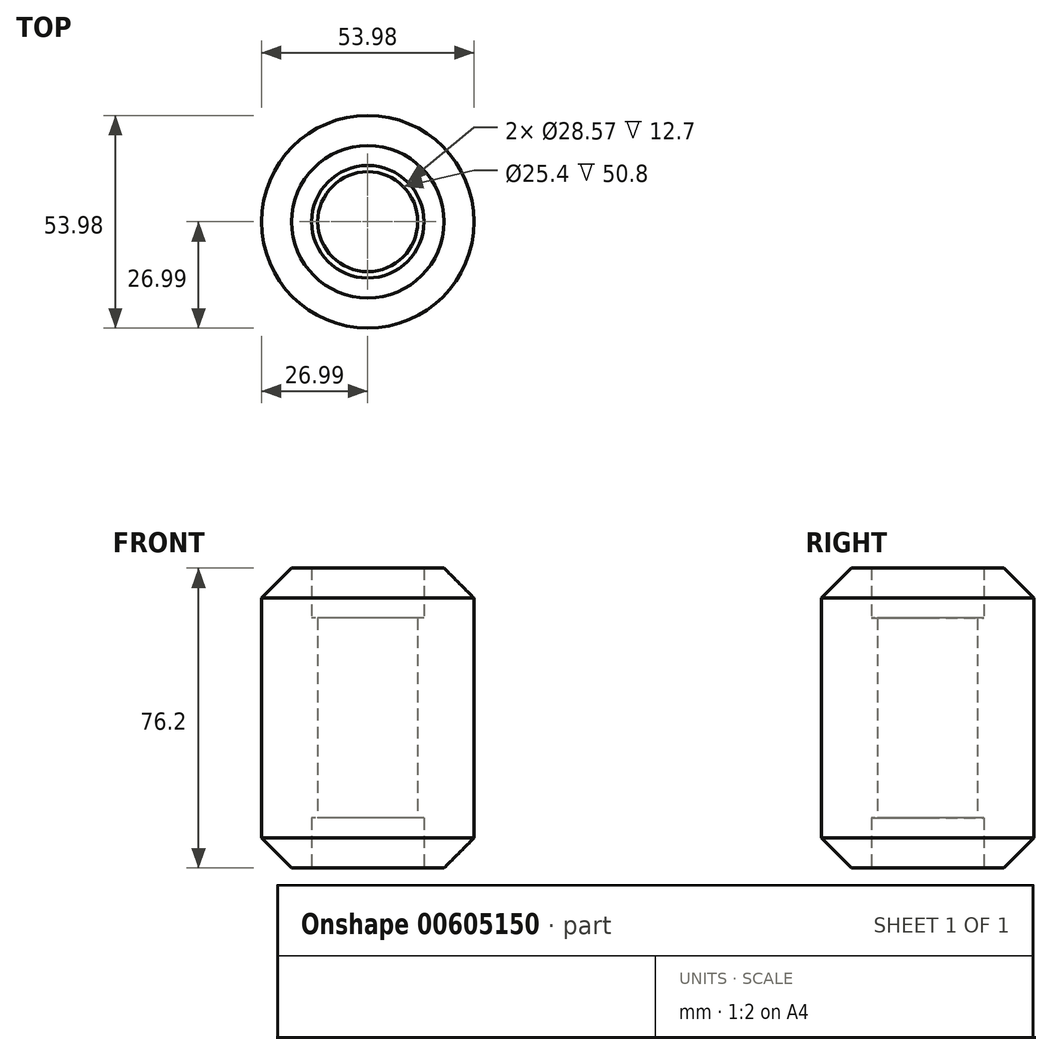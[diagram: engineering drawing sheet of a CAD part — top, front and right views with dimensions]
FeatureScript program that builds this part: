
annotation { "Feature Type Name" : "Feature", "Feature Type Description" : "" }
export const myFeature = defineFeature(function(context is Context, id is Id, definition is map)
    precondition{}
    {
        {
            var Q0;
            Q0=qCreatedBy(makeId("Top.planeOp"),FACE);
            var sketch = newSketch(context, id + "F0", { "sketchPlane" : qUnion([Q0])});
            skLineSegment(sketch, "E0", {"start": v(0, 0) * mm, "end": v(12.7, 0) * mm});
            skCircle(sketch, "E1", {"center": v(0, 0) * mm, "radius": 12.7 * mm});
            skCircle(sketch, "E2.0", {"center": v(0, 0) * mm, "radius": 14.29 * mm});
            skSolve(sketch);
        }
        {
            var Q0;
            Q0=qCreatedBy(makeId("Top.planeOp"),FACE);
            var sketch = newSketch(context, id + "F1", { "sketchPlane" : qUnion([Q0])});
            skSolve(sketch);
        }
        {
            var Q0;
            Q0=qSketchRegion(id+"F1",true);
            var Q1;
            Q1=makeQuery(id+"F0.imprint","IMPRINT",FACE,{"disambiguationData":[TD([[makeQuery(id+"F0.imprint","IMPRINT",EDGE,{"derivedFrom":sQuery(id+"F0.wireOp",EDGE,"E1")}),-1.0]])]});
            extrude(context, id + "F2", {"entities" : qUnion([Q0, Q1]), "depth" : 50.8 * mm, "offsetDistance" : 25.4 * mm});
        }
        {
            var Q0;
            Q0=qSketchRegion(id+"F0",true);
            var sketch = newSketch(context, id + "F3", { "sketchPlane" : qUnion([Q0])});
            skCircle(sketch, "E3.0", {"center": v(0, 0) * mm, "radius": 26.99 * mm});
            skSolve(sketch);
        }
        {
            var Q0;
            Q0=makeQuery(id+"F3.imprint","IMPRINT",FACE,{"disambiguationData":[TD([[makeQuery(id+"F3.imprint","IMPRINT",EDGE,{"derivedFrom":sQuery(id+"F3.wireOp",EDGE,"E3.0")}),1.0]])]});
            var Q1;
            Q1=sQuery(id+"F0.wireOp",EDGE,"E2.0");
            var Q2;
            Q2=sQuery(id+"F3.wireOp",EDGE,"E3.0");
            extrude(context, id + "F4", {"entities" : qUnion([Q0]), "operationType" : NewBodyOperationType.ADD, "surfaceEntities" : qUnion([Q1, Q2]), "depth" : 63.5 * mm, "offsetDistance" : 25.4 * mm, "hasSecondDirection" : true, "secondDirectionOppositeDirection" : true, "secondDirectionDepth" : 12.7 * mm});
        }
        {
            var Q0;
            Q0=makeQuery(id+"F4.opExtrude","CAP_EDGE",EDGE,{"disambiguationData":[OSD([sQuery(id+"F3.wireOp",EDGE,"E3.0")])],"isStart":false});
            var Q1;
            Q1=makeQuery(id+"F4.opExtrude","CAP_EDGE",EDGE,{"disambiguationData":[OSD([sQuery(id+"F3.wireOp",EDGE,"E3.0")])],"isStart":true});
            chamfer(context, id + "F5", {"entities" : qUnion([Q0, Q1]), "width" : 7.62 * mm, "tangentPropagation" : true});
        }
    });
